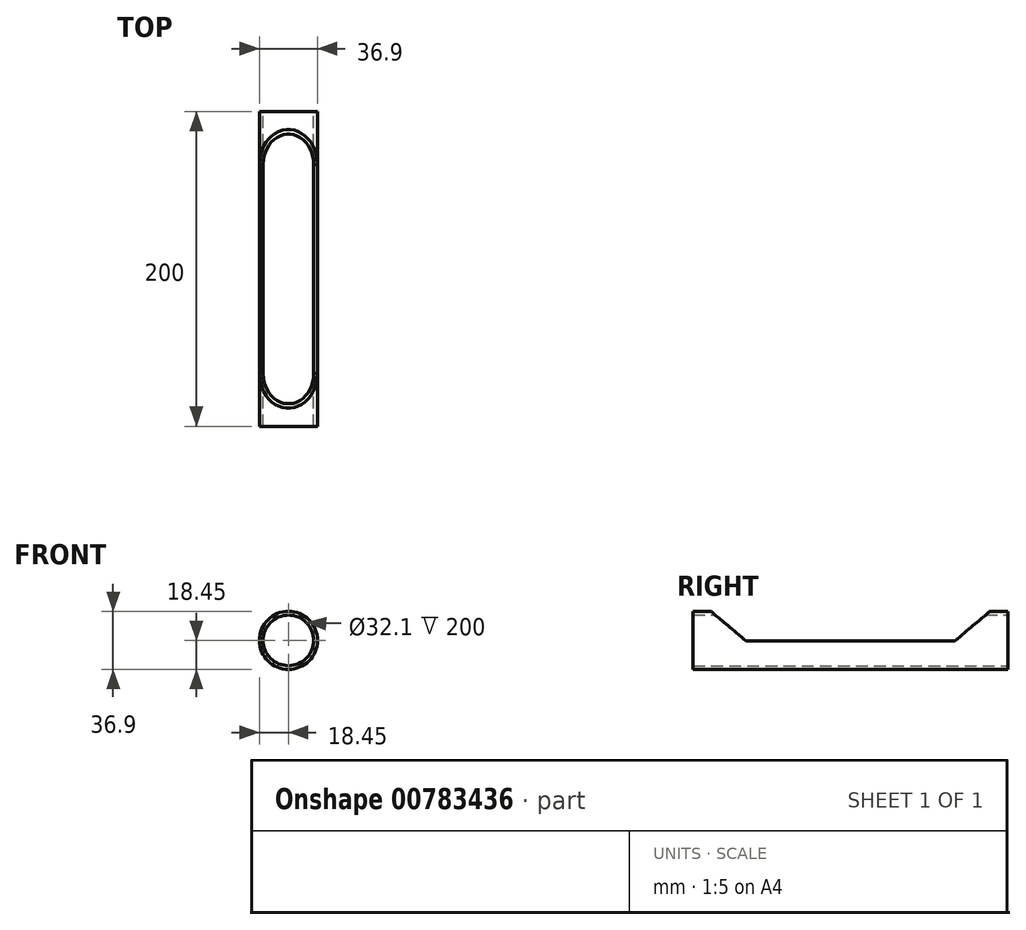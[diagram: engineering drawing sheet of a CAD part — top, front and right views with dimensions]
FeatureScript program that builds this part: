
annotation { "Feature Type Name" : "Feature", "Feature Type Description" : "" }
export const myFeature = defineFeature(function(context is Context, id is Id, definition is map)
    precondition{}
    {
        {
            var Q0;
            Q0=qCreatedBy(makeId("Front.planeOp"),FACE);
            var sketch = newSketch(context, id + "F0", { "sketchPlane" : qUnion([Q0])});
            skCircle(sketch, "E0", {"center": v(0, 0) * mm, "radius": 18.45 * mm});
            skCircle(sketch, "E1", {"center": v(0, 0) * mm, "radius": 16.05 * mm});
            skLineSegment(sketch, "E2.bottom", {"start": v(18.45, -18.45) * mm, "end": v(-18.45, -18.45) * mm});
            skLineSegment(sketch, "E2.top", {"start": v(18.45, 18.45) * mm, "end": v(-18.45, 18.45) * mm});
            skLineSegment(sketch, "E2.left", {"start": v(18.45, -18.45) * mm, "end": v(18.45, 18.45) * mm});
            skLineSegment(sketch, "E2.right", {"start": v(-18.45, -18.45) * mm, "end": v(-18.45, 18.45) * mm});
            skLineSegment(sketch, "E3", {"start": v(0, 0) * mm, "end": v(0, 18.45) * mm});
            skLineSegment(sketch, "E4", {"start": v(0, 0) * mm, "end": v(0, -18.45) * mm});
            skLineSegment(sketch, "E5", {"start": v(0, 0) * mm, "end": v(-15.98, 9.22) * mm});
            skLineSegment(sketch, "E6", {"start": v(0, 0) * mm, "end": v(15.98, 9.23) * mm});
            skSolve(sketch);
        }
        {
            var Q0;
            {var subQ3=sQuery(id+"F0.wireOp",EDGE,"CAZaTLFN-tJie-LHG7-8vTy-squ8jarRoMMn");var subQ5=sQuery(id+"F0.wireOp",EDGE,"E1");var subQ6=makeQuery(id+"F0.imprint","INTERSECT",VERTEX,{"derivedFrom":[subQ5,subQ3]});Q0=makeQuery(id+"F0.imprint","IMPRINT",FACE,{"disambiguationData":[TD([[makeQuery(id+"F0.imprint","IMPRINT",EDGE,{"disambiguationData":[TD([[subQ6,1.0]])],"derivedFrom":subQ5}),-1.0]])]});}
            var Q1;
            {var subQ3=sQuery(id+"F0.wireOp",EDGE,"CAZaTLFN-tJie-LHG7-8vTy-squ8jarRoMMn");var subQ5=sQuery(id+"F0.wireOp",EDGE,"E1");var subQ6=makeQuery(id+"F0.imprint","INTERSECT",VERTEX,{"derivedFrom":[subQ5,subQ3]});Q1=makeQuery(id+"F0.imprint","IMPRINT",FACE,{"disambiguationData":[TD([[makeQuery(id+"F0.imprint","IMPRINT",EDGE,{"disambiguationData":[TD([[subQ6,-1.0]])],"derivedFrom":subQ5}),-1.0]])]});}
            var Q2;
            {var subQ0=sQuery(id+"F0.wireOp",EDGE,"l8s0sOfb-fzFU-R0BE-n0NO-c75pVUIZOnGM");var subQ1=sQuery(id+"F0.wireOp",EDGE,"E0");var subQ2=makeQuery(id+"F0.imprint","INTERSECT",VERTEX,{"derivedFrom":[subQ1,subQ0]});Q2=makeQuery(id+"F0.imprint","IMPRINT",FACE,{"disambiguationData":[TD([[makeQuery(id+"F0.imprint","IMPRINT",EDGE,{"disambiguationData":[TD([[subQ2,1.0]])],"derivedFrom":subQ1}),1.0]])]});}
            var Q3;
            {var subQ0=sQuery(id+"F0.wireOp",EDGE,"4xxhsBqu-Dr4I-gKWc-ZI2R-gIkBFB4eemaq");var subQ1=sQuery(id+"F0.wireOp",EDGE,"E0");var subQ2=makeQuery(id+"F0.imprint","INTERSECT",VERTEX,{"derivedFrom":[subQ1,subQ0]});Q3=makeQuery(id+"F0.imprint","IMPRINT",FACE,{"disambiguationData":[TD([[makeQuery(id+"F0.imprint","IMPRINT",EDGE,{"disambiguationData":[TD([[subQ2,-1.0]])],"derivedFrom":subQ1}),1.0]])]});}
            var Q4;
            Q4=sQuery(id+"F0.wireOp",EDGE,"E0");
            extrude(context, id + "F1", {"entities" : qUnion([Q0, Q1, Q2, Q3]), "surfaceEntities" : qUnion([Q4]), "depth" : 100 * mm, "offsetDistance" : 25.4 * mm, "hasSecondDirection" : true, "secondDirectionOppositeDirection" : true, "secondDirectionDepth" : 100 * mm});
        }
        {
            var Q0;
            Q0=qCreatedBy(makeId("Right.planeOp"),FACE);
            var sketch = newSketch(context, id + "F2", { "sketchPlane" : qUnion([Q0])});
            skLineSegment(sketch, "E7.bottom", {"start": v(88.6, -0.25) * mm, "end": v(-88.6, -0.25) * mm});
            skLineSegment(sketch, "E7.top", {"start": v(88.6, 37.15) * mm, "end": v(-88.6, 37.15) * mm});
            skLineSegment(sketch, "E7.left", {"start": v(88.6, -0.25) * mm, "end": v(88.6, 37.15) * mm});
            skLineSegment(sketch, "E7.right", {"start": v(-88.6, -0.25) * mm, "end": v(-88.6, 37.15) * mm});
            skPoint(sketch, "E7.middle", {"position": v(0, 18.45) * mm});
            skLineSegment(sketch, "E8", {"start": v(-100, 18.45) * mm, "end": v(100, 18.45) * mm});
            skLineSegment(sketch, "E9", {"start": v(100, -18.45) * mm, "end": v(-100, -18.45) * mm});
            skLineSegment(sketch, "E10", {"start": v(88.6, 18.45) * mm, "end": v(66.31, -0.25) * mm});
            skLineSegment(sketch, "E11.MirrorCS", {"start": v(-88.6, 18.45) * mm, "end": v(-66.31, -0.25) * mm});
            skSolve(sketch);
        }
        {
            var Q0;
            {var subQ0=sQuery(id+"F2.wireOp",EDGE,"E7.top");Q0=makeQuery(id+"F2.imprint","IMPRINT",FACE,{"disambiguationData":[TD([[makeQuery(id+"F2.imprint","IMPRINT",EDGE,{"derivedFrom":subQ0}),1.0]])]});}
            var Q1;
            {var subQ0=sQuery(id+"F2.wireOp",EDGE,"E10");Q1=makeQuery(id+"F2.imprint","IMPRINT",FACE,{"disambiguationData":[TD([[makeQuery(id+"F2.imprint","IMPRINT",EDGE,{"derivedFrom":subQ0}),-1.0]])]});}
            extrude(context, id + "F3", {"entities" : qUnion([Q0, Q1]), "operationType" : NewBodyOperationType.REMOVE, "oppositeDirection" : true, "depth" : 50.8 * mm, "offsetDistance" : 25.4 * mm, "hasSecondDirection" : true, "secondDirectionOppositeDirection" : false, "secondDirectionDepth" : 50.8 * mm});
        }
    });
